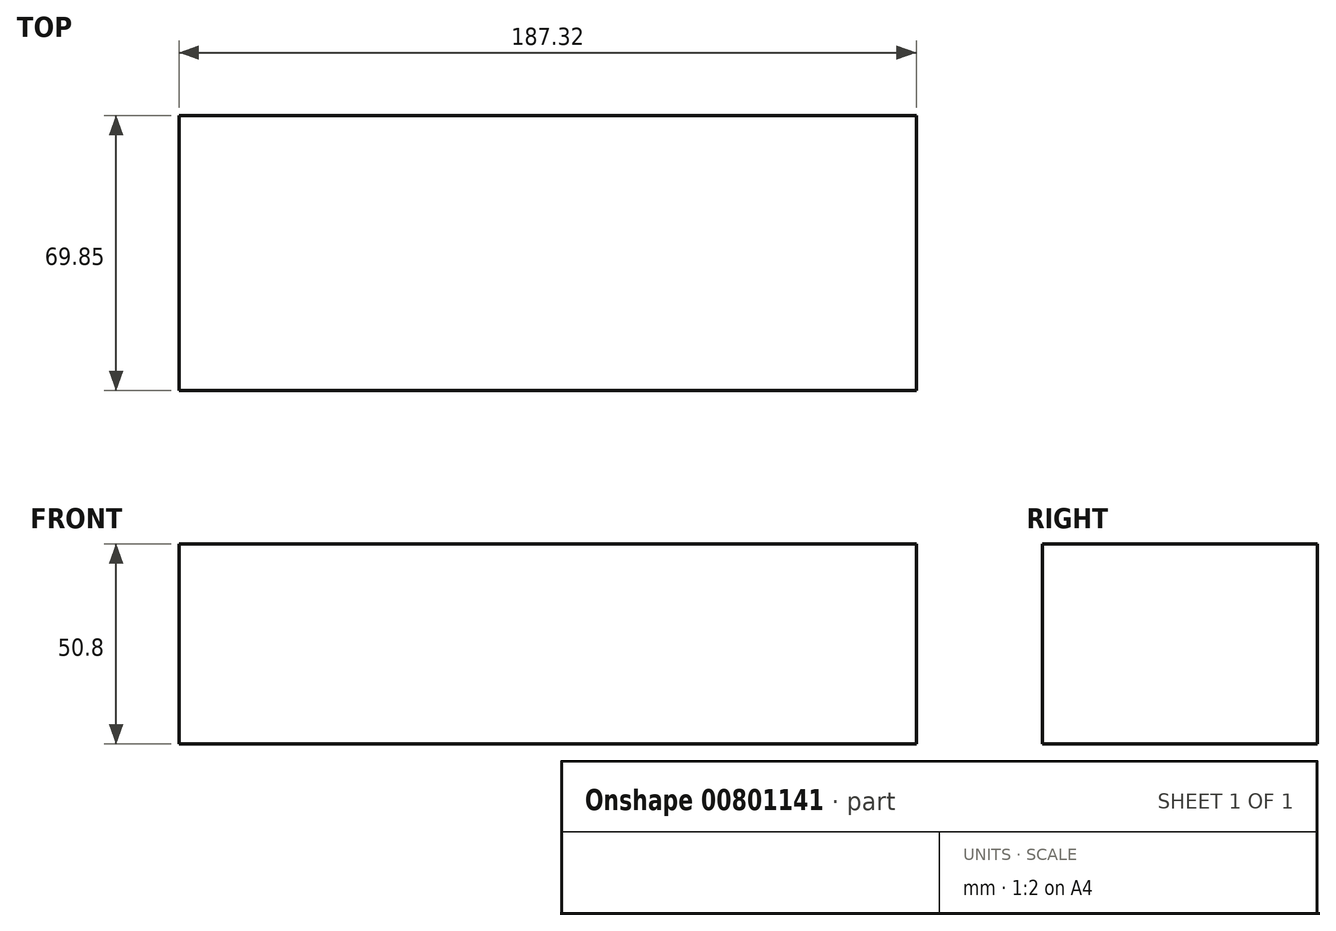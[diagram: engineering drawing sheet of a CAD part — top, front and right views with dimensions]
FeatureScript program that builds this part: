
annotation { "Feature Type Name" : "Feature", "Feature Type Description" : "" }
export const myFeature = defineFeature(function(context is Context, id is Id, definition is map)
    precondition{}
    {
        {
            var Q0;
            Q0=qCreatedBy(makeId("Top.planeOp"),FACE);
            var sketch = newSketch(context, id + "F0", { "sketchPlane" : qUnion([Q0])});
            skLineSegment(sketch, "E0", {"start": v(0, 0) * mm, "end": v(187.33, 0) * mm});
            skLineSegment(sketch, "E1", {"start": v(187.33, 0) * mm, "end": v(187.33, 69.85) * mm});
            skLineSegment(sketch, "E2", {"start": v(187.33, 69.85) * mm, "end": v(0, 69.85) * mm});
            skLineSegment(sketch, "E3", {"start": v(0, 69.85) * mm, "end": v(0, 0) * mm});
            skSolve(sketch);
        }
        {
            var Q0;
            Q0=makeQuery(id+"F0.imprint","IMPRINT",FACE,{"disambiguationData":[TD([[makeQuery(id+"F0.imprint","IMPRINT",EDGE,{"derivedFrom":sQuery(id+"F0.wireOp",EDGE,"E0")}),1.0]])]});
            extrude(context, id + "F1", {"entities" : qUnion([Q0]), "depth" : 50.8 * mm, "offsetDistance" : 25.4 * mm});
        }
    });
